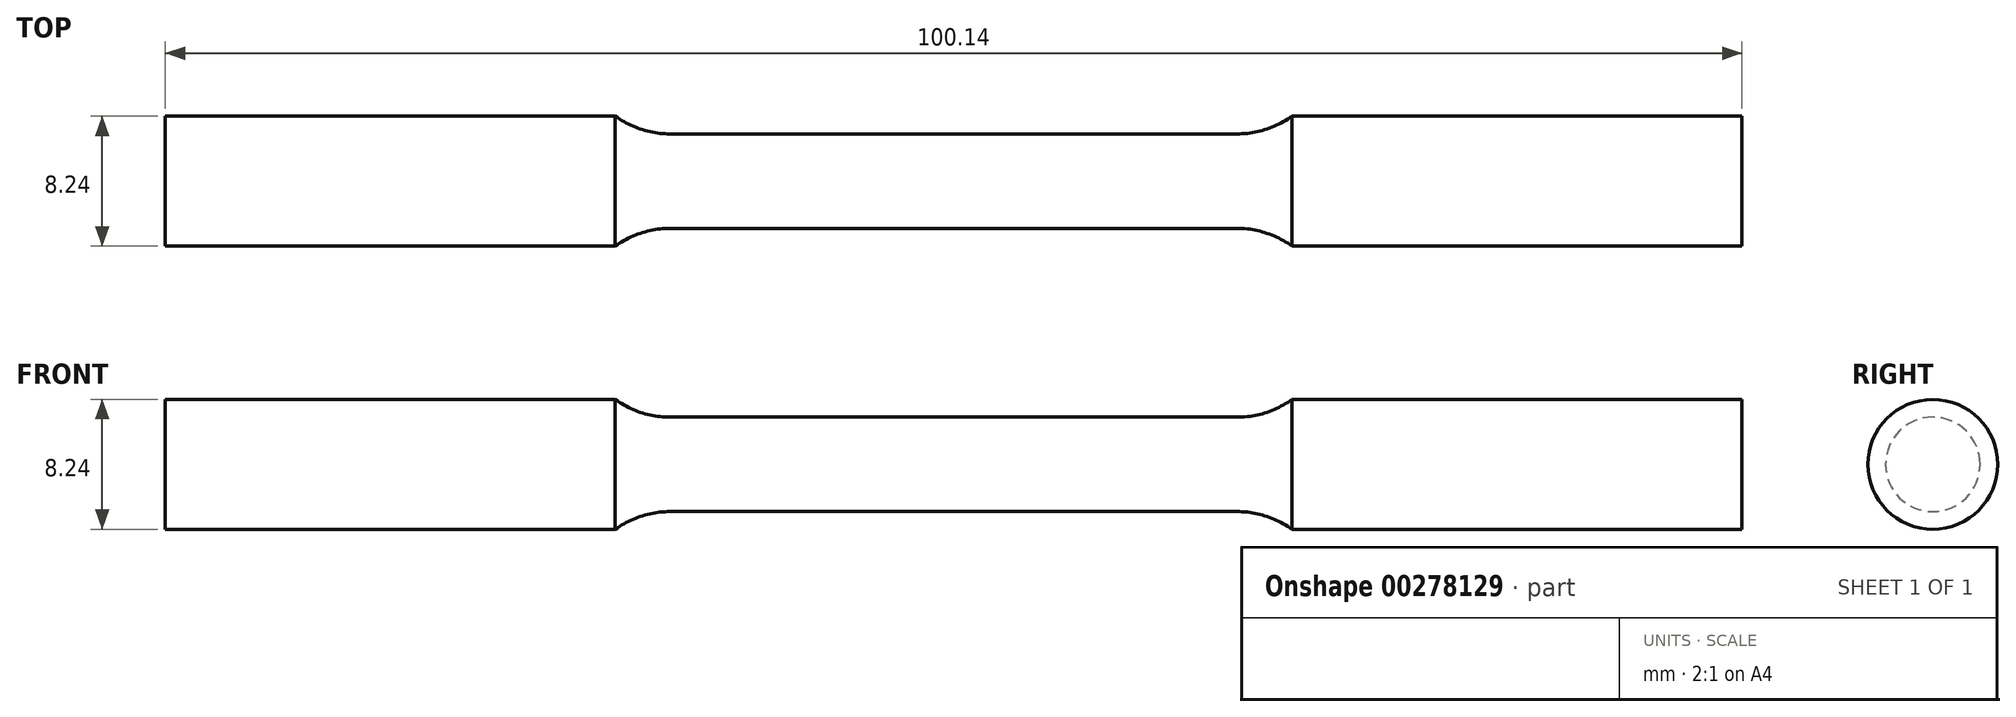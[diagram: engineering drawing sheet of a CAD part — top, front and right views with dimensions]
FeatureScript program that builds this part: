
annotation { "Feature Type Name" : "Feature", "Feature Type Description" : "" }
export const myFeature = defineFeature(function(context is Context, id is Id, definition is map)
    precondition{}
    {
        {
            var Q0;
            Q0=qCreatedBy(makeId("Front.planeOp"),FACE);
            var sketch = newSketch(context, id + "F0", { "sketchPlane" : qUnion([Q0])});
            skLineSegment(sketch, "E0", {"start": v(0, 3) * mm, "end": v(18, 3) * mm});
            skArc(sketch, "E1", {"start": v(18, 3) * mm, "mid": v(19.83, 3.29) * mm, "end": v(21.49, 4.12) * mm});
            skLineSegment(sketch, "E2", {"start": v(21.49, 4.12) * mm, "end": v(50.07, 4.12) * mm});
            skLineSegment(sketch, "E3", {"start": v(50.07, 4.12) * mm, "end": v(50.07, 0) * mm});
            skLineSegment(sketch, "E4.MirrorCS", {"start": v(0, 3) * mm, "end": v(-18, 3) * mm});
            skLineSegment(sketch, "E5.MirrorCS", {"start": v(-50.07, 4.12) * mm, "end": v(-50.07, 0) * mm});
            skLineSegment(sketch, "E6.MirrorCS", {"start": v(-21.49, 4.12) * mm, "end": v(-50.07, 4.12) * mm});
            skArc(sketch, "E7.MirrorCS", {"start": v(-18, 3) * mm, "mid": v(-19.83, 3.29) * mm, "end": v(-21.49, 4.12) * mm});
            skLineSegment(sketch, "E8", {"start": v(-50.07, 0) * mm, "end": v(50.07, 0) * mm});
            skSolve(sketch);
        }
        {
            var Q0;
            Q0 = qSketchRegion(id + "F0", true);
            var Q1;
            Q1=sQuery(id+"F0.wireOp",EDGE,"E8");
            revolve(context, id + "F1", {"entities" : qUnion([Q0]), "axis" : qUnion([Q1]), "revolveType" : RevolveType.FULL});
        }
    });
